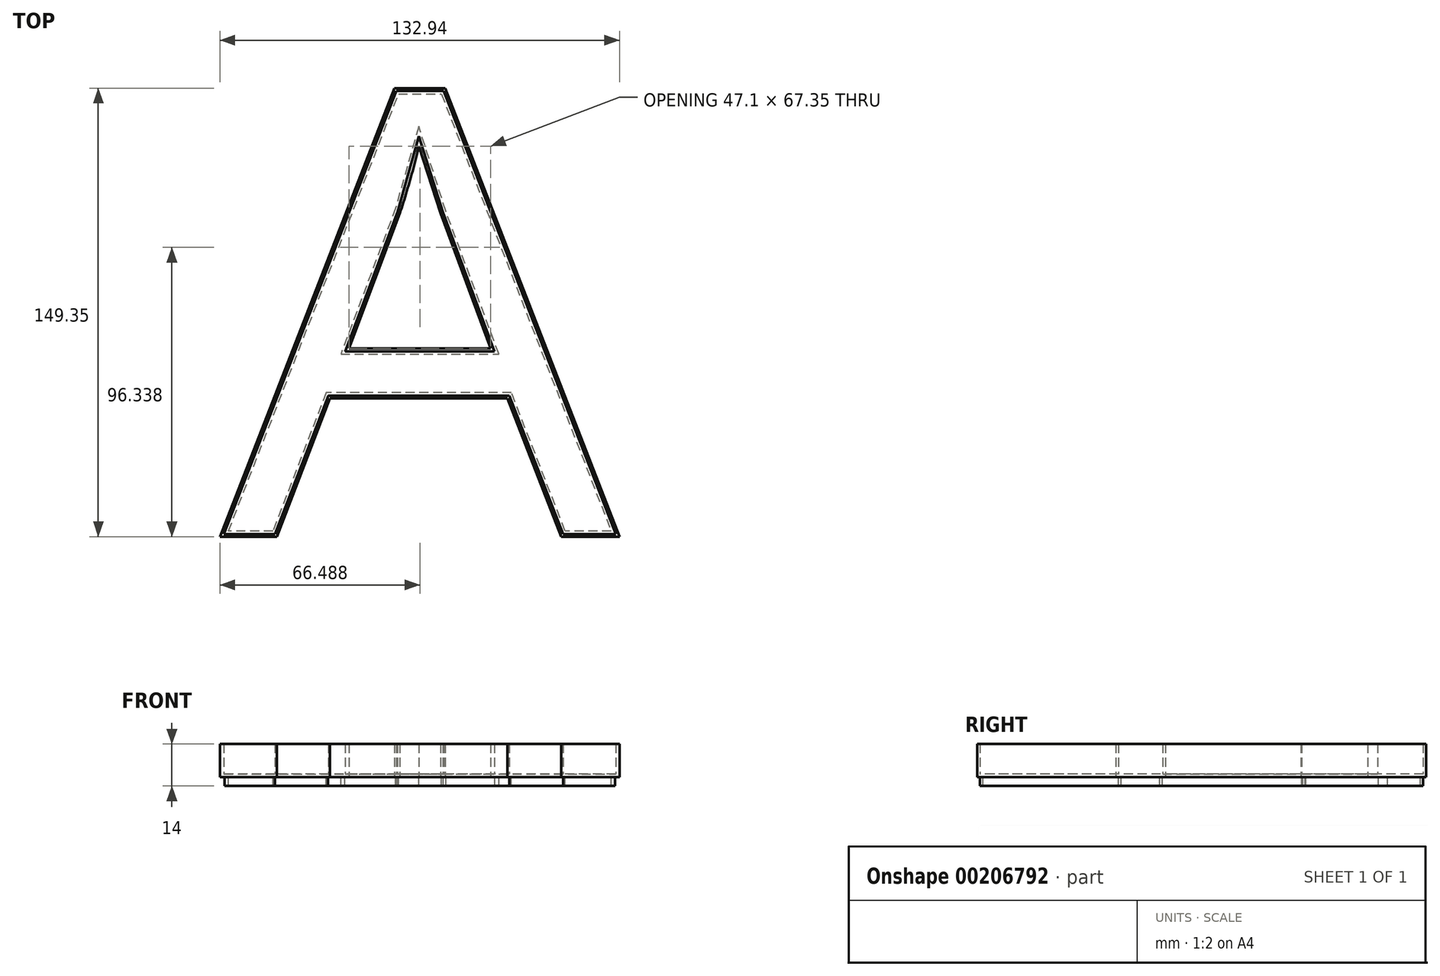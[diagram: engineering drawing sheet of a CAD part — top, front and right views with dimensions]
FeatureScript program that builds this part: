
annotation { "Feature Type Name" : "Feature", "Feature Type Description" : "" }
export const myFeature = defineFeature(function(context is Context, id is Id, definition is map)
    precondition{}
    {
        {
            var Q0;
            Q0=qCreatedBy(makeId("Top.planeOp"),FACE);
            var sketch = newSketch(context, id + "F0", { "sketchPlane" : qUnion([Q0])});
            skText(sketch, "E0", { "text": "A", "fontName": "NotoSans-Regular.ttf"});
            const initialGuessF0  = {"E0": [-0.08416, -0.05264, 1, 0, 0.15]};
            skSetInitialGuess(sketch, initialGuessF0);
            skSolve(sketch);
        }
        {
            var Q0;
            Q0=makeQuery(id+"F0.imprint","IMPRINT",FACE,{"disambiguationData":[TD([[makeQuery(id+"F0.imprint","IMPRINT",EDGE,{"derivedFrom":sQuery(id+"F0.wireOp",EDGE,"E0.sketch_text.stroke-0")}),-1.0]])]});
            extrude(context, id + "F1", {"entities" : qUnion([Q0]), "depth" : 1 * mm, "offsetDistance" : 25 * mm});
        }
        {
            var Q0;
            Q0=makeQuery(id+"F1.opExtrude","CAP_FACE",FACE,{"disambiguationData":[OSD([sQuery(id+"F0.wireOp",EDGE,"E0.sketch_text.stroke-0"),sQuery(id+"F0.wireOp",EDGE,"E0.sketch_text.stroke-1"),sQuery(id+"F0.wireOp",EDGE,"E0.sketch_text.stroke-2"),sQuery(id+"F0.wireOp",EDGE,"E0.sketch_text.stroke-3"),sQuery(id+"F0.wireOp",EDGE,"E0.sketch_text.stroke-4"),sQuery(id+"F0.wireOp",EDGE,"E0.sketch_text.stroke-5"),sQuery(id+"F0.wireOp",EDGE,"E0.sketch_text.stroke-6"),sQuery(id+"F0.wireOp",EDGE,"E0.sketch_text.stroke-7"),sQuery(id+"F0.wireOp",EDGE,"E0.sketch_text.stroke-8"),sQuery(id+"F0.wireOp",EDGE,"E0.sketch_text.stroke-9"),sQuery(id+"F0.wireOp",EDGE,"E0.sketch_text.stroke-10"),sQuery(id+"F0.wireOp",EDGE,"E0.sketch_text.stroke-11"),sQuery(id+"F0.wireOp",EDGE,"E0.sketch_text.stroke-12")])],"isStart":false});
            var sketch = newSketch(context, id + "F2", { "sketchPlane" : qUnion([Q0])});
            skLineSegment(sketch, "E1.0", {"start": v(7.17, 9.12) * mm, "end": v(-9.97, 55.37) * mm});
            skLineSegment(sketch, "E1.1", {"start": v(-42.53, 9.12) * mm, "end": v(7.17, 9.12) * mm});
            skLineSegment(sketch, "E1.2", {"start": v(-9.97, 55.37) * mm, "end": v(-18.06, 80.67) * mm});
            skLineSegment(sketch, "E1.4", {"start": v(-25.18, 55.37) * mm, "end": v(-42.53, 9.12) * mm});
            skLineSegment(sketch, "E2", {"start": v(-18.06, 80.67) * mm, "end": v(-25.18, 55.37) * mm});
            skLineSegment(sketch, "E3.0", {"start": v(-65.87, -51.74) * mm, "end": v(-82.85, -51.74) * mm});
            skLineSegment(sketch, "E3.1", {"start": v(-48.16, -5.65) * mm, "end": v(-65.87, -51.74) * mm});
            skLineSegment(sketch, "E3.2", {"start": v(-82.85, -51.74) * mm, "end": v(-25.48, 95.8) * mm});
            skLineSegment(sketch, "E3.3", {"start": v(12.09, -5.65) * mm, "end": v(-48.16, -5.65) * mm});
            skLineSegment(sketch, "E3.4", {"start": v(-25.48, 95.8) * mm, "end": v(-9.81, 95.8) * mm});
            skLineSegment(sketch, "E3.5", {"start": v(-9.81, 95.8) * mm, "end": v(47.46, -51.74) * mm});
            skLineSegment(sketch, "E3.6", {"start": v(47.46, -51.74) * mm, "end": v(30, -51.74) * mm});
            skLineSegment(sketch, "E3.7", {"start": v(30, -51.74) * mm, "end": v(12.09, -5.65) * mm});
            skSolve(sketch);
        }
        {
            var Q0;
            Q0=makeQuery(id+"F2.imprint","IMPRINT",FACE,{"disambiguationData":[TD([[makeQuery(id+"F2.imprint","IMPRINT",EDGE,{"derivedFrom":sQuery(id+"F2.wireOp",EDGE,"E1.0")}),1.0]])]});
            var Q1;
            Q1=makeQuery(id+"F2.imprint","IMPRINT",FACE,{"disambiguationData":[TD([[makeQuery(id+"F2.imprint","IMPRINT",EDGE,{"derivedFrom":sQuery(id+"F2.wireOp",EDGE,"E3.0")}),1.0]])]});
            extrude(context, id + "F3", {"entities" : qUnion([Q0, Q1]), "operationType" : NewBodyOperationType.ADD, "depth" : 10 * mm, "offsetDistance" : 25 * mm});
        }
        {
            var Q0;
            Q0 = qSketchRegion(id + "F0", true);
            extrude(context, id + "F4", {"entities" : qUnion([Q0]), "depth" : 1 * mm, "offsetDistance" : 25 * mm});
        }
        {
            var Q0;
            Q0=makeQuery(id+"F1.opExtrude","CAP_FACE",FACE,{"disambiguationData":[OSD([sQuery(id+"F0.wireOp",EDGE,"E0.sketch_text.stroke-0"),sQuery(id+"F0.wireOp",EDGE,"E0.sketch_text.stroke-1"),sQuery(id+"F0.wireOp",EDGE,"E0.sketch_text.stroke-2"),sQuery(id+"F0.wireOp",EDGE,"E0.sketch_text.stroke-3"),sQuery(id+"F0.wireOp",EDGE,"E0.sketch_text.stroke-4"),sQuery(id+"F0.wireOp",EDGE,"E0.sketch_text.stroke-5"),sQuery(id+"F0.wireOp",EDGE,"E0.sketch_text.stroke-6"),sQuery(id+"F0.wireOp",EDGE,"E0.sketch_text.stroke-7"),sQuery(id+"F0.wireOp",EDGE,"E0.sketch_text.stroke-8"),sQuery(id+"F0.wireOp",EDGE,"E0.sketch_text.stroke-9"),sQuery(id+"F0.wireOp",EDGE,"E0.sketch_text.stroke-10"),sQuery(id+"F0.wireOp",EDGE,"E0.sketch_text.stroke-11"),sQuery(id+"F0.wireOp",EDGE,"E0.sketch_text.stroke-12")])],"isStart":true});
            var sketch = newSketch(context, id + "F5", { "sketchPlane" : qUnion([Q0])});
            skLineSegment(sketch, "E4.0", {"start": v(-65.94, 51.64) * mm, "end": v(-82.7, 51.64) * mm});
            skLineSegment(sketch, "E4.1", {"start": v(-48.23, 5.55) * mm, "end": v(-65.94, 51.64) * mm});
            skLineSegment(sketch, "E4.2", {"start": v(-82.7, 51.64) * mm, "end": v(-25.4, -95.7) * mm});
            skLineSegment(sketch, "E4.3", {"start": v(12.16, 5.55) * mm, "end": v(-48.23, 5.55) * mm});
            skLineSegment(sketch, "E4.4", {"start": v(-25.4, -95.7) * mm, "end": v(-9.88, -95.7) * mm});
            skLineSegment(sketch, "E4.5", {"start": v(-9.88, -95.7) * mm, "end": v(47.32, 51.64) * mm});
            skLineSegment(sketch, "E4.6", {"start": v(47.32, 51.64) * mm, "end": v(30.06, 51.64) * mm});
            skLineSegment(sketch, "E4.7", {"start": v(30.06, 51.64) * mm, "end": v(12.16, 5.55) * mm});
            skLineSegment(sketch, "E5.0", {"start": v(-66.56, 50.74) * mm, "end": v(-81.39, 50.74) * mm});
            skLineSegment(sketch, "E5.1", {"start": v(-48.85, 4.65) * mm, "end": v(-66.56, 50.74) * mm});
            skLineSegment(sketch, "E5.2", {"start": v(-81.39, 50.74) * mm, "end": v(-24.8, -94.8) * mm});
            skLineSegment(sketch, "E5.3", {"start": v(12.77, 4.65) * mm, "end": v(-48.85, 4.65) * mm});
            skLineSegment(sketch, "E5.4", {"start": v(-24.8, -94.8) * mm, "end": v(-10.5, -94.8) * mm});
            skLineSegment(sketch, "E5.5", {"start": v(-10.5, -94.8) * mm, "end": v(46, 50.74) * mm});
            skLineSegment(sketch, "E5.6", {"start": v(46, 50.74) * mm, "end": v(30.68, 50.74) * mm});
            skLineSegment(sketch, "E5.7", {"start": v(30.68, 50.74) * mm, "end": v(12.77, 4.65) * mm});
            skLineSegment(sketch, "E6.1", {"start": v(-9.88, -55.4) * mm, "end": v(-18.01, -80.84) * mm});
            skLineSegment(sketch, "E6.2", {"start": v(-24.86, -56.51) * mm, "end": v(-42.67, -9.02) * mm});
            skLineSegment(sketch, "E6.3", {"start": v(-42.67, -9.02) * mm, "end": v(7.31, -9.02) * mm});
            skLineSegment(sketch, "E6.4", {"start": v(7.31, -9.02) * mm, "end": v(-9.88, -55.4) * mm});
            skLineSegment(sketch, "E7", {"start": v(-18.01, -80.84) * mm, "end": v(-24.86, -56.51) * mm});
            skLineSegment(sketch, "E8.0", {"start": v(-25.72, -56.8) * mm, "end": v(-43.97, -8.12) * mm});
            skLineSegment(sketch, "E8.1", {"start": v(-18.07, -83.97) * mm, "end": v(-25.72, -56.8) * mm});
            skLineSegment(sketch, "E8.2", {"start": v(-43.97, -8.12) * mm, "end": v(8.6, -8.12) * mm});
            skLineSegment(sketch, "E8.3", {"start": v(8.6, -8.12) * mm, "end": v(-9.03, -55.7) * mm});
            skLineSegment(sketch, "E8.4", {"start": v(-9.03, -55.7) * mm, "end": v(-18.07, -83.97) * mm});
            skSolve(sketch);
        }
        {
            var Q0;
            Q0=makeQuery(id+"F5.imprint","IMPRINT",FACE,{"disambiguationData":[TD([[makeQuery(id+"F5.imprint","IMPRINT",EDGE,{"derivedFrom":sQuery(id+"F5.wireOp",EDGE,"E4.0")}),1.0]])]});
            var Q1;
            Q1=makeQuery(id+"F5.imprint","IMPRINT",FACE,{"disambiguationData":[TD([[makeQuery(id+"F5.imprint","IMPRINT",EDGE,{"derivedFrom":sQuery(id+"F5.wireOp",EDGE,"E6.1")}),1.0]])]});
            extrude(context, id + "F6", {"entities" : qUnion([Q0, Q1]), "operationType" : NewBodyOperationType.ADD, "depth" : 3 * mm, "offsetDistance" : 25 * mm});
        }
    });
